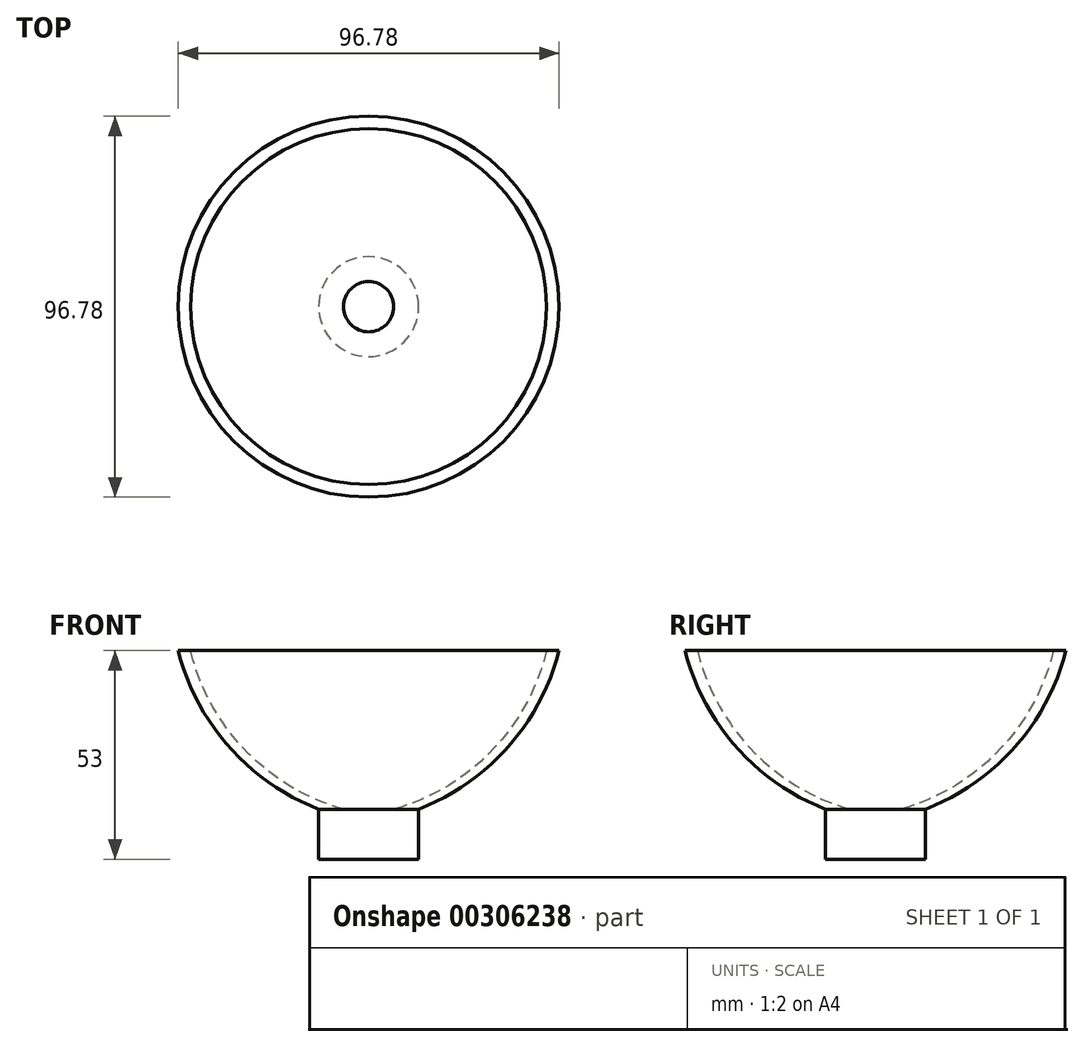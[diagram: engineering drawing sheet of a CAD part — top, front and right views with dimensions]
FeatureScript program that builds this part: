
annotation { "Feature Type Name" : "Feature", "Feature Type Description" : "" }
export const myFeature = defineFeature(function(context is Context, id is Id, definition is map)
    precondition{}
    {
        {
            var Q0;
            Q0=qCreatedBy(makeId("Front.planeOp"),FACE);
            var sketch = newSketch(context, id + "F0", { "sketchPlane" : qUnion([Q0])});
            skLineSegment(sketch, "E0", {"start": v(-20.4, -12.7) * mm, "end": v(-20.4, 0) * mm});
            skArc(sketch, "E1", {"start": v(-20.4, 0) * mm, "mid": v(2.33, 15.83) * mm, "end": v(15.3, 40.3) * mm});
            skLineSegment(sketch, "E2", {"start": v(15.3, 40.3) * mm, "end": v(12.13, 40.3) * mm});
            skArc(sketch, "E3", {"start": v(-26.7, 0) * mm, "mid": v(-1.82, 14.88) * mm, "end": v(12.13, 40.3) * mm});
            skLineSegment(sketch, "E4", {"start": v(-20.4, -12.7) * mm, "end": v(-33.1, -12.7) * mm});
            skLineSegment(sketch, "E5", {"start": v(-33.1, -12.7) * mm, "end": v(-33.1, 0) * mm});
            skLineSegment(sketch, "E6", {"start": v(-33.1, 0) * mm, "end": v(-26.7, 0) * mm});
            skSolve(sketch);
        }
        {
            var Q0;
            Q0 = qSketchRegion(id + "F0", true);
            var Q1;
            Q1=sQuery(id+"F0.wireOp",EDGE,"E5");
            revolve(context, id + "F1", {"entities" : qUnion([Q0]), "axis" : qUnion([Q1]), "revolveType" : RevolveType.FULL});
        }
    });
